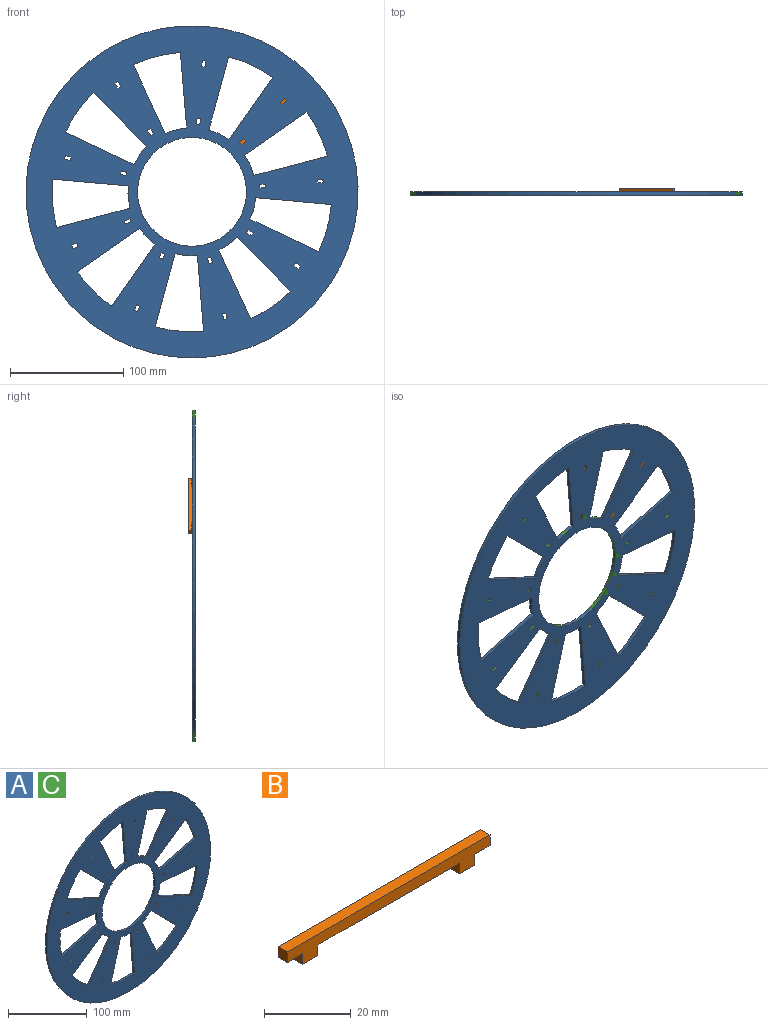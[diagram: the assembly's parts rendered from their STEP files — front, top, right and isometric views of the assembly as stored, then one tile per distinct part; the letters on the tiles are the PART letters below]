
ASSEMBLY  parts=3 mates=1
PART A: 112 faces, bbox 293x3x293 mm
  f0: plane 4.11x3mm, normal (-0.82,0,-0.57), area 15mm2, adj f1,f109,f110,f111
  f1: plane 3x2.46mm, normal (-0.57,0,0.82), area 9mm2, adj f0,f2,f110,f111
  f2: plane 4.11x3mm, normal (0.82,0,0.57), area 15mm2, adj f1,f109,f110,f111
  f3: plane 4.11x3mm, normal (-0.82,0,-0.57), area 15mm2, adj f4,f81,f110,f111
  f4: plane 3x2.46mm, normal (-0.57,0,0.82), area 9mm2, adj f3,f5,f110,f111
  f5: plane 4.11x3mm, normal (0.82,0,0.57), area 15mm2, adj f4,f81,f110,f111
  f6: plane 3.55x3.52mm, normal (-0.7,0,0.71), area 15mm2, adj f7,f82,f110,f111
  f7: plane 3x2.13mm, normal (0.71,0,0.7), area 9mm2, adj f6,f8,f110,f111
  f8: plane 3.55x3.52mm, normal (0.7,0,-0.71), area 15mm2, adj f7,f82,f110,f111
  f9: plane 3x2.13mm, normal (-0.71,0,-0.7), area 9mm2, adj f10,f83,f110,f111
  f10: plane 3.55x3.52mm, normal (-0.7,0,0.71), area 15mm2, adj f9,f11,f110,f111
  f11: plane 3x2.13mm, normal (0.71,0,0.7), area 9mm2, adj f10,f83,f110,f111
  f12: plane 4.08x3mm, normal (-0.58,0,-0.82), area 15mm2, adj f13,f84,f110,f111
  f13: plane 3x2.45mm, normal (-0.82,0,0.58), area 9mm2, adj f12,f14,f110,f111
  f14: plane 4.08x3mm, normal (0.58,0,0.82), area 15mm2, adj f13,f84,f110,f111
  f15: plane 4.08x3mm, normal (-0.58,0,-0.82), area 15mm2, adj f16,f85,f110,f111
  f16: plane 3x2.45mm, normal (-0.82,0,0.58), area 9mm2, adj f15,f17,f110,f111
  f17: plane 4.08x3mm, normal (0.58,0,0.82), area 15mm2, adj f16,f85,f110,f111
  f18: plane 3x2.71mm, normal (0.43,0,0.9), area 9mm2, adj f19,f86,f110,f111
  f19: plane 4.52x3mm, normal (0.9,0,-0.43), area 15mm2, adj f18,f20,f110,f111
  f20: plane 3x2.71mm, normal (-0.43,0,-0.9), area 9mm2, adj f19,f86,f110,f111
  f21: plane 4.52x3mm, normal (0.9,0,-0.43), area 15mm2, adj f22,f87,f110,f111
  f22: plane 3x2.71mm, normal (-0.43,0,-0.9), area 9mm2, adj f21,f23,f110,f111
  f23: plane 4.52x3mm, normal (-0.9,0,0.43), area 15mm2, adj f22,f87,f110,f111
  f24: plane 3x2.89mm, normal (-0.96,0,0.26), area 9mm2, adj f25,f88,f110,f111
  f25: plane 4.82x3mm, normal (0.26,0,0.96), area 15mm2, adj f24,f26,f110,f111
  f26: plane 3x2.89mm, normal (0.96,0,-0.26), area 9mm2, adj f25,f88,f110,f111
  f27: plane 4.82x3mm, normal (-0.26,0,-0.96), area 15mm2, adj f28,f89,f110,f111
  f28: plane 3x2.89mm, normal (-0.96,0,0.26), area 9mm2, adj f27,f29,f110,f111
  f29: plane 4.82x3mm, normal (0.26,0,0.96), area 15mm2, adj f28,f89,f110,f111
  f30: plane 66.72x6.1mm, normal (-0.09,0,-1), area 201mm2, adj f31,f90,f110,f111
  f31: cylinder r=56.5mm len=19.55mm, axis (0,1,0), area 59.2mm2, adj f30,f32,f110,f111
  f32: plane 64.78x17.09mm, normal (-0.26,0,0.97), area 201mm2, adj f31,f90,f110,f111
  f33: cylinder r=123.5mm len=30.45mm, axis (0,1,0), area 129.3mm2, adj f34,f93,f110,f111
  f34: plane 55.03x38.22mm, normal (0.57,0,-0.82), area 201mm2, adj f33,f35,f110,f111
  f35: cylinder r=56.5mm len=13.93mm, axis (0,1,0), area 59.2mm2, adj f34,f93,f110,f111
  f36: cylinder r=123.5mm len=42.71mm, axis (0,1,0), area 129.3mm2, adj f37,f94,f110,f111
  f37: plane 64.65x17.59mm, normal (0.96,0,-0.26), area 201mm2, adj f36,f38,f110,f111
  f38: cylinder r=56.5mm len=19.54mm, axis (0,1,0), area 59.2mm2, adj f37,f94,f110,f111
  f39: cylinder r=123.5mm len=35.23mm, axis (0,1,0), area 129.3mm2, adj f40,f95,f110,f111
  f40: plane 60.83x28.08mm, normal (0.91,0,0.42), area 201mm2, adj f39,f41,f110,f111
  f41: cylinder r=56.5mm len=16.12mm, axis (0,1,0), area 59.2mm2, adj f40,f95,f110,f111
  f42: cylinder r=123.5mm len=41.39mm, axis (0,1,0), area 129.3mm2, adj f43,f96,f110,f111
  f43: plane 60.61x28.55mm, normal (0.43,0,0.9), area 201mm2, adj f42,f44,f110,f111
  f44: cylinder r=56.5mm len=18.93mm, axis (0,1,0), area 59.2mm2, adj f43,f96,f110,f111
  f45: cylinder r=123.5mm len=38.94mm, axis (0,1,0), area 129.3mm2, adj f46,f97,f110,f111
  f46: plane 64.78x17.09mm, normal (-0.26,0,0.97), area 201mm2, adj f45,f47,f110,f111
  f47: cylinder r=56.5mm len=17.82mm, axis (0,1,0), area 59.2mm2, adj f46,f97,f110,f111
  f48: cylinder r=123.5mm len=38.8mm, axis (0,1,0), area 129.3mm2, adj f49,f98,f110,f111
  f49: plane 54.73x38.64mm, normal (-0.82,0,0.58), area 201mm2, adj f48,f50,f110,f111
  f50: cylinder r=56.5mm len=17.75mm, axis (0,1,0), area 59.2mm2, adj f49,f98,f110,f111
  f51: cylinder r=123.5mm len=41.47mm, axis (0,1,0), area 129.3mm2, adj f52,f99,f110,f111
  f52: plane 66.77x5.58mm, normal (-1,0,-0.08), area 201mm2, adj f51,f53,f110,f111
  f53: cylinder r=56.5mm len=18.97mm, axis (0,1,0), area 59.2mm2, adj f52,f99,f110,f111
  f54: cylinder r=123.5mm len=35.04mm, axis (0,1,0), area 129.3mm2, adj f55,f100,f110,f111
  f55: plane 47.56x47.19mm, normal (-0.71,0,-0.7), area 201mm2, adj f54,f56,f110,f111
  f56: cylinder r=56.5mm len=16.03mm, axis (0,1,0), area 59.2mm2, adj f55,f100,f110,f111
  f57: plane 3x2.72mm, normal (-0.91,0,-0.42), area 9mm2, adj f58,f101,f110,f111
  f58: plane 4.54x3mm, normal (-0.42,0,0.91), area 15mm2, adj f57,f59,f110,f111
  f59: plane 3x2.72mm, normal (0.91,0,0.42), area 9mm2, adj f58,f101,f110,f111
  f60: plane 3x2.72mm, normal (-0.91,0,-0.42), area 9mm2, adj f61,f102,f110,f111
  f61: plane 4.54x3mm, normal (-0.42,0,0.91), area 15mm2, adj f60,f62,f110,f111
  f62: plane 3x2.72mm, normal (0.91,0,0.42), area 9mm2, adj f61,f102,f110,f111
  f63: plane 3x2.9mm, normal (0.26,0,-0.97), area 9mm2, adj f64,f103,f110,f111
  f64: plane 4.83x3mm, normal (-0.97,0,-0.26), area 15mm2, adj f63,f65,f110,f111
  f65: plane 3x2.9mm, normal (-0.26,0,0.97), area 9mm2, adj f64,f103,f110,f111
  f66: plane 3x2.9mm, normal (0.26,0,-0.97), area 9mm2, adj f67,f104,f110,f111
  f67: plane 4.83x3mm, normal (-0.97,0,-0.26), area 15mm2, adj f66,f68,f110,f111
  f68: plane 3x2.9mm, normal (-0.26,0,0.97), area 9mm2, adj f67,f104,f110,f111
  f69: plane 3x2.99mm, normal (1,0,0.08), area 9mm2, adj f70,f105,f110,f111
  f70: plane 4.98x3mm, normal (0.08,0,-1), area 15mm2, adj f69,f71,f110,f111
  f71: plane 3x2.99mm, normal (-1,0,-0.08), area 9mm2, adj f70,f105,f110,f111
  f72: plane 3x2.99mm, normal (1,0,0.08), area 9mm2, adj f73,f106,f110,f111
  f73: plane 4.98x3mm, normal (0.08,0,-1), area 15mm2, adj f72,f74,f110,f111
  f74: plane 3x2.99mm, normal (-1,0,-0.08), area 9mm2, adj f73,f106,f110,f111
  f75: plane 3x2.99mm, normal (-0.09,0,-1), area 9mm2, adj f76,f107,f110,f111
  f76: plane 4.98x3mm, normal (-1,0,0.09), area 15mm2, adj f75,f77,f110,f111
  f77: plane 3x2.99mm, normal (0.09,0,1), area 9mm2, adj f76,f107,f110,f111
  f78: plane 3x2.99mm, normal (-0.09,0,-1), area 9mm2, adj f79,f108,f110,f111
  f79: plane 4.98x3mm, normal (-1,0,0.09), area 15mm2, adj f78,f80,f110,f111
  f80: plane 3x2.99mm, normal (0.09,0,1), area 9mm2, adj f79,f108,f110,f111
  f81: plane 3x2.46mm, normal (0.57,0,-0.82), area 9mm2, adj f3,f5,f110,f111
  f82: plane 3x2.13mm, normal (-0.71,0,-0.7), area 9mm2, adj f6,f8,f110,f111
  f83: plane 3.55x3.52mm, normal (0.7,0,-0.71), area 15mm2, adj f9,f11,f110,f111
  f84: plane 3x2.45mm, normal (0.82,0,-0.58), area 9mm2, adj f12,f14,f110,f111
  f85: plane 3x2.45mm, normal (0.82,0,-0.58), area 9mm2, adj f15,f17,f110,f111
  f86: plane 4.52x3mm, normal (-0.9,0,0.43), area 15mm2, adj f18,f20,f110,f111
  f87: plane 3x2.71mm, normal (0.43,0,0.9), area 9mm2, adj f21,f23,f110,f111
  f88: plane 4.82x3mm, normal (-0.26,0,-0.96), area 15mm2, adj f24,f26,f110,f111
  f89: plane 3x2.89mm, normal (0.96,0,-0.26), area 9mm2, adj f27,f29,f110,f111
  f90: cylinder r=123.5mm len=42.74mm, axis (0,1,0), area 129.3mm2, adj f30,f32,f110,f111
  f91: cylinder r=146.5mm len=293mm, axis (0,1,0), area 2761.5mm2, adj f110,f111
  f92: cylinder r=48mm len=96mm, axis (0,1,0), area 904.8mm2, adj f110,f111
  f93: plane 54.73x38.64mm, normal (-0.82,0,0.58), area 201mm2, adj f33,f35,f110,f111
  f94: plane 66.77x5.58mm, normal (-1,0,-0.08), area 201mm2, adj f36,f38,f110,f111
  f95: plane 47.56x47.19mm, normal (-0.71,0,-0.7), area 201mm2, adj f39,f41,f110,f111
  f96: plane 66.72x6.1mm, normal (-0.09,0,-1), area 201mm2, adj f42,f44,f110,f111
  f97: plane 55.03x38.22mm, normal (0.57,0,-0.82), area 201mm2, adj f45,f47,f110,f111
  f98: plane 64.65x17.59mm, normal (0.96,0,-0.26), area 201mm2, adj f48,f50,f110,f111
  f99: plane 60.83x28.08mm, normal (0.91,0,0.42), area 201mm2, adj f51,f53,f110,f111
  f100: plane 60.61x28.55mm, normal (0.43,0,0.9), area 201mm2, adj f54,f56,f110,f111
  f101: plane 4.54x3mm, normal (0.42,0,-0.91), area 15mm2, adj f57,f59,f110,f111
  f102: plane 4.54x3mm, normal (0.42,0,-0.91), area 15mm2, adj f60,f62,f110,f111
  f103: plane 4.83x3mm, normal (0.97,0,0.26), area 15mm2, adj f63,f65,f110,f111
  f104: plane 4.83x3mm, normal (0.97,0,0.26), area 15mm2, adj f66,f68,f110,f111
  f105: plane 4.98x3mm, normal (-0.08,0,1), area 15mm2, adj f69,f71,f110,f111
  f106: plane 4.98x3mm, normal (-0.08,0,1), area 15mm2, adj f72,f74,f110,f111
  f107: plane 4.98x3mm, normal (1,0,-0.09), area 15mm2, adj f75,f77,f110,f111
  f108: plane 4.98x3mm, normal (1,0,-0.09), area 15mm2, adj f78,f80,f110,f111
  f109: plane 3x2.46mm, normal (0.57,0,-0.82), area 9mm2, adj f0,f2,f110,f111
  f110: plane 293x293mm, normal (0,-1,0), area 40973.6mm2, adj f0,f1,f2,f3,f4,f5,f6,f7
  f111: plane 293x293mm, normal (0,1,0), area 40973.6mm2, adj f0,f1,f2,f3,f4,f5,f6,f7
PART B: 14 faces, bbox 66x3x6 mm
  f0: plane 3x3mm, normal (-1,0,0), area 9mm2, adj f1,f11,f12,f13
  f1: plane 5x3mm, normal (0,0,-1), area 15mm2, adj f0,f2,f12,f13
  f2: plane 3x3mm, normal (-1,0,0), area 9mm2, adj f1,f3,f12,f13
  f3: plane 5x3mm, normal (0,0,-1), area 15mm2, adj f2,f4,f12,f13
  f4: plane 3x3mm, normal (1,0,0), area 9mm2, adj f3,f5,f12,f13
  f5: plane 46x3mm, normal (0,0,-1), area 138mm2, adj f4,f6,f12,f13
  f6: plane 3x3mm, normal (-1,0,0), area 9mm2, adj f5,f7,f12,f13
  f7: plane 5x3mm, normal (0,0,-1), area 15mm2, adj f6,f8,f12,f13
  f8: plane 3x3mm, normal (1,0,0), area 9mm2, adj f7,f9,f12,f13
  f9: plane 5x3mm, normal (0,0,-1), area 15mm2, adj f8,f10,f12,f13
  f10: plane 3x3mm, normal (1,0,0), area 9mm2, adj f9,f11,f12,f13
  f11: plane 66x3mm, normal (0,0,1), area 198mm2, adj f0,f10,f12,f13
  f12: plane 66x6mm, normal (0,-1,0), area 228mm2, adj f0,f1,f2,f3,f4,f5,f6,f7
  f13: plane 66x6mm, normal (0,1,0), area 228mm2, adj f0,f1,f2,f3,f4,f5,f6,f7
PART C: same geometry as A
PLACE A at identity
PLACE B rot(axis=(-0.86,-0.36,-0.36),98.3deg) t=(62.09,-13.44,59.5)mm
PLACE C at identity
MATE fastened B.f8 <-> C.f82  axis (-0.71,0,-0.7) through (82.34,-1.5,81.71)mm
